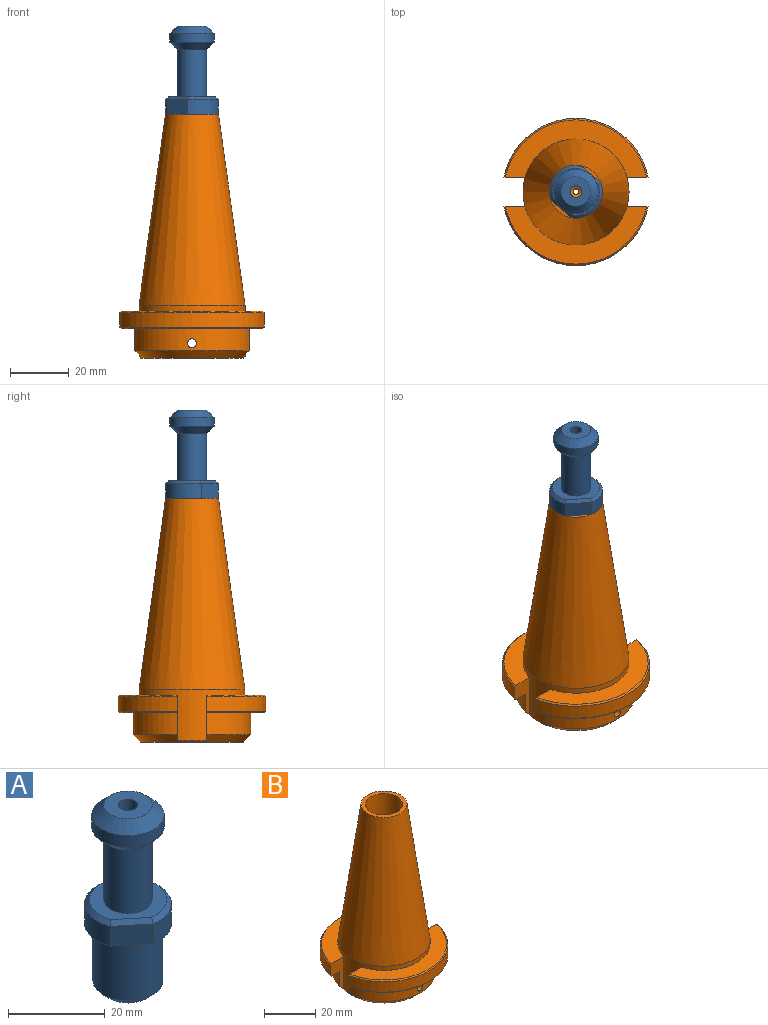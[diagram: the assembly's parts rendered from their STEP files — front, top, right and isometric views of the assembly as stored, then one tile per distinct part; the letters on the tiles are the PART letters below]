
ASSEMBLY  parts=2 mates=1
PART A: 19 faces, bbox 18x18x46.5 mm
  f0: plane 16x16mm, normal (0,0,1), area 108.7mm2, adj f6,f15,f16,f17,f18
  f1: cylinder r=9mm len=12.16mm, axis (0,0,1), area 94.2mm2, adj f8,f13,f14,f15
  f2: plane 10x10mm, normal (0,0,1), area 66mm2, adj f3,f12
  f3: cone r=7.5mm half-angle=45deg, axis (0,0,-1), area 138.8mm2, adj f2,f4
  f4: cylinder r=7.5mm len=15mm, axis (0,0,1), area 141.4mm2, adj f3,f5
  f5: cone r=5mm half-angle=45deg, axis (0,0,1), area 138.8mm2, adj f4,f6
  f6: cylinder r=5mm len=16mm, axis (0,0,1), area 502.7mm2, adj f0,f5
  f7: cylinder r=9mm len=12.16mm, axis (0,0,1), area 94.2mm2, adj f8,f13,f14,f18
  f8: plane 18x18mm, normal (0,0,-1), area 74.7mm2, adj f1,f7,f9,f13,f14
  f9: cylinder r=7.25mm len=14.5mm, axis (0,0,1), area 660.5mm2, adj f8,f11
  f10: plane 10.5x10.5mm, normal (0,0,-1), area 74mm2, adj f11,f12
  f11: cone r=7.25mm half-angle=45deg, axis (0,0,1), area 111.1mm2, adj f9,f10
  f12: cylinder r=2mm len=46.5mm, axis (0,0,-1), area 584.3mm2, adj f2,f10
  f13: plane 6.95x5.72mm, normal (0.64,0.77,0), area 45mm2, adj f1,f7,f8,f16
  f14: plane 6.95x5.72mm, normal (-0.64,-0.77,0), area 45mm2, adj f1,f7,f8,f17
  f15: cone r=8mm half-angle=45deg, axis (0,0,-1), area 24.8mm2, adj f0,f1,f16,f17
  f16: plane 7.38x6.33mm, normal (0.45,0.55,0.71), area 12.3mm2, adj f0,f13,f15,f18
  f17: plane 7.38x6.33mm, normal (-0.45,-0.55,0.71), area 12.3mm2, adj f0,f14,f15,f18
  f18: cone r=8mm half-angle=45deg, axis (0,0,-1), area 24.8mm2, adj f0,f7,f16,f17
PART B: 28 faces, bbox 49x50x82.8 mm
  f0: cone r=0mm half-angle=59deg, axis (0,0,1), area 189mm2, adj f20,f27
  f1: cylinder r=1.5mm len=40mm, axis (0,1,0), area 327.6mm2, adj f2,f10,f11,f12,f13,f27
  f2: cylinder r=20mm len=38.73mm, axis (0,0,1), area 388.4mm2, adj f1,f6,f7,f23,f25
  f3: plane 47.97x19.5mm, normal (0,0,1), area 368.3mm2, adj f16,f21,f24,f26
  f4: plane 47.97x19.5mm, normal (0,0,1), area 368.3mm2, adj f8,f16,f23,f25
  f5: cylinder r=25mm len=48.99mm, axis (0,0,1), area 338.9mm2, adj f8,f9,f23,f25
  f6: plane 47.97x19.5mm, normal (0,0,-1), area 269.2mm2, adj f2,f9,f23,f25
  f7: cone r=20mm half-angle=45deg, axis (0,0,1), area 359.2mm2, adj f2,f10,f16,f19,f23,f24,f25,f26
  f8: cone r=24.5mm half-angle=45deg, axis (0,0,-1), area 47.9mm2, adj f4,f5,f23,f25
  f9: cone r=25mm half-angle=45deg, axis (0,0,1), area 47.9mm2, adj f5,f6,f23,f25
  f10: cylinder r=20mm len=38.73mm, axis (0,0,1), area 388.4mm2, adj f1,f7,f18,f24,f26
  f11: cylinder r=5mm len=10mm, axis (0,0,-1), area 149.9mm2, adj f1,f12,f13,f19
  f12: plane 9.54x3.5mm, normal (0,0,-1), area 24.5mm2, adj f1,f11
  f13: plane 9.54x3.5mm, normal (0,0,-1), area 24.5mm2, adj f1,f11
  f14: plane 18x18mm, normal (0,0,1), area 89.3mm2, adj f15,f20
  f15: cone r=18mm half-angle=7.9deg, axis (0,0,-1), area 5549.3mm2, adj f14,f16
  f16: cylinder r=18mm len=36mm, axis (0,0,1), area 539.3mm2, adj f3,f4,f7,f15,f23,f24,f25,f26
  f17: cylinder r=25mm len=48.99mm, axis (0,0,1), area 338.9mm2, adj f21,f22,f24,f26
  f18: plane 47.97x19.5mm, normal (0,0,-1), area 269.2mm2, adj f10,f22,f24,f26
  f19: plane 35x35mm, normal (0,0,-1), area 883.6mm2, adj f7,f11
  f20: cylinder r=7.25mm len=19.5mm, axis (0,0,1), area 888.3mm2, adj f0,f14
  f21: cone r=24.5mm half-angle=45deg, axis (0,0,-1), area 47.9mm2, adj f3,f17,f24,f26
  f22: cone r=25mm half-angle=45deg, axis (0,0,1), area 47.9mm2, adj f17,f18,f24,f26
  f23: plane 15.48x7.23mm, normal (0,-1,0), area 60.2mm2, adj f2,f4,f5,f6,f7,f8,f9,f16
  f24: plane 15.48x7.23mm, normal (0,1,0), area 60.2mm2, adj f3,f7,f10,f16,f17,f18,f21,f22
  f25: plane 15.48x7.23mm, normal (0,-1,0), area 60.2mm2, adj f2,f4,f5,f6,f7,f8,f9,f16
  f26: plane 15.48x7.23mm, normal (0,1,0), area 60.2mm2, adj f3,f7,f10,f16,f17,f18,f21,f22
  f27: cylinder r=1mm len=53.38mm, axis (0,0,-1), area 334.1mm2, adj f0,f1
PLACE A t=(-7.8,0.09,58.8)mm
PLACE B t=(-7.8,0.09,-7.45)mm
MATE fastened A.f1 <-> B.f0  axis (0,0,1) through (-7.8,0.09,75.3)mm
